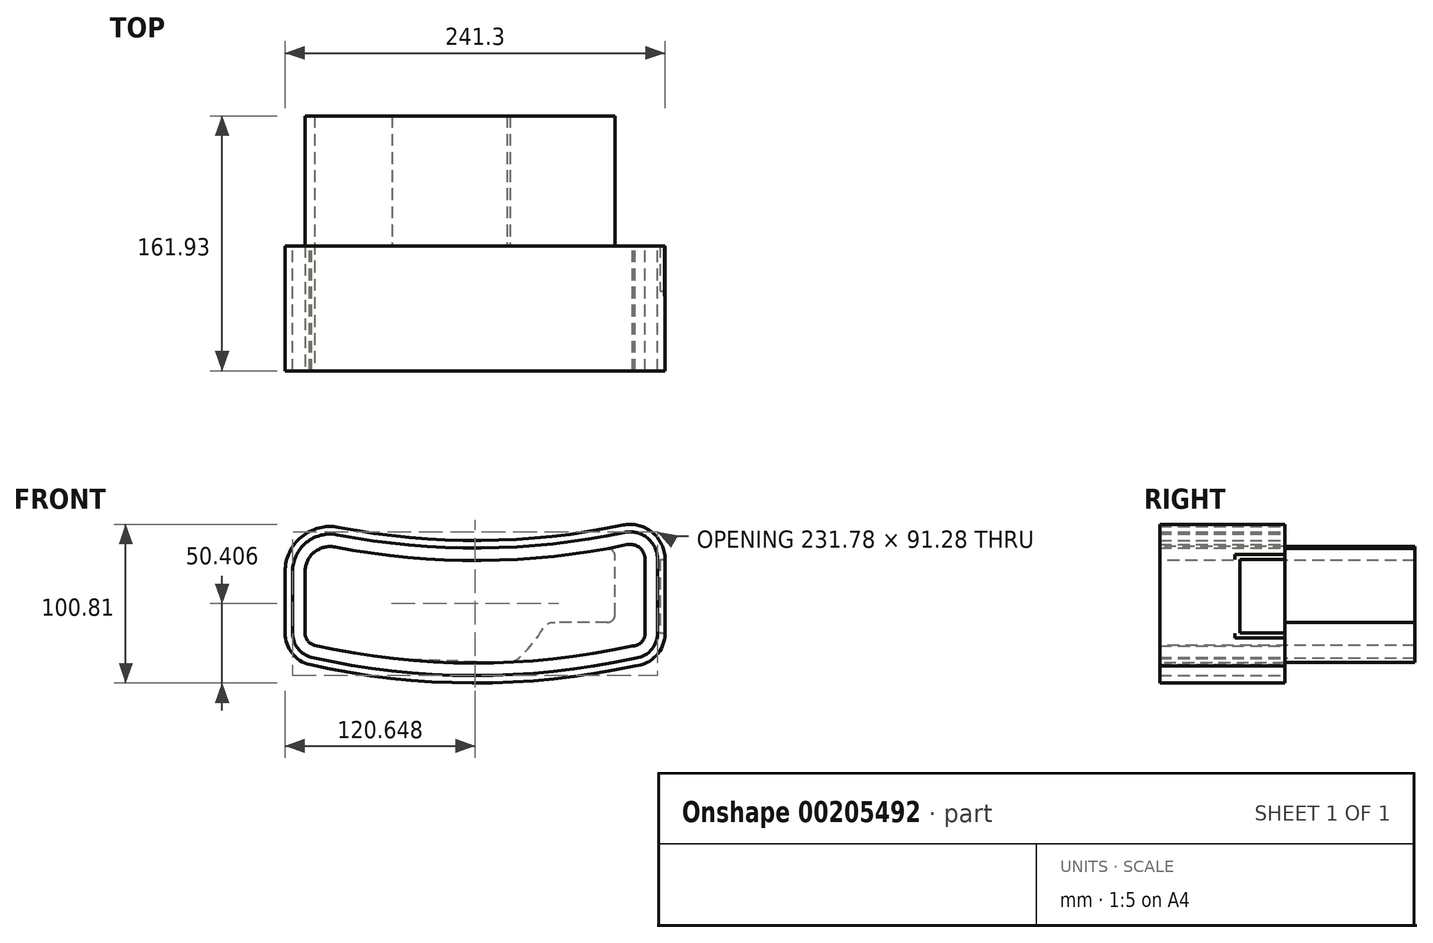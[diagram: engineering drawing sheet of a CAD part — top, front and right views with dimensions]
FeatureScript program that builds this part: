
annotation { "Feature Type Name" : "Feature", "Feature Type Description" : "" }
export const myFeature = defineFeature(function(context is Context, id is Id, definition is map)
    precondition{}
    {
        {
            var Q0;
            Q0=qCreatedBy(makeId("Front.planeOp"),FACE);
            var sketch = newSketch(context, id + "F0", { "sketchPlane" : qUnion([Q0])});
            skLineSegment(sketch, "E0", {"start": v(-57.08, 54.83) * mm, "end": v(-57.08, -10.26) * mm, "construction": true});
            skLineSegment(sketch, "E1", {"start": v(-57.08, 54.83) * mm, "end": v(158.82, 54.83) * mm, "construction": true});
            skLineSegment(sketch, "E2", {"start": v(50.87, 54.83) * mm, "end": v(50.87, 42.13) * mm, "construction": true});
            skArc(sketch, "E3", {"start": v(-57.08, 54.83) * mm, "mid": v(50.87, 42.13) * mm, "end": v(158.82, 54.83) * mm, "construction": true});
            skLineSegment(sketch, "E4", {"start": v(50.87, 42.13) * mm, "end": v(50.87, -22.96) * mm, "construction": true});
            skLineSegment(sketch, "E5", {"start": v(158.82, 54.83) * mm, "end": v(158.82, -10.26) * mm, "construction": true});
            skLineSegment(sketch, "E6", {"start": v(50.87, 42.13) * mm, "end": v(50.87, 13.56) * mm, "construction": true});
            skLineSegment(sketch, "E7", {"start": v(158.82, 22.29) * mm, "end": v(158.82, 9.59) * mm, "construction": true});
            skLineSegment(sketch, "E8", {"start": v(158.82, 9.59) * mm, "end": v(50.87, 13.56) * mm, "construction": true});
            skLineSegment(sketch, "E9", {"start": v(50.87, 13.56) * mm, "end": v(-57.08, 17.52) * mm, "construction": true});
            skLineSegment(sketch, "E10", {"start": v(-57.08, 35.15) * mm, "end": v(-57.08, -3.95) * mm});
            skLineSegment(sketch, "E11", {"start": v(158.82, 42.92) * mm, "end": v(158.82, -4.16) * mm});
            skArc(sketch, "E12", {"start": v(-38.17, 50.73) * mm, "mid": v(54.65, 42.15) * mm, "end": v(147.32, 52.24) * mm});
            skPoint(sketch, "E13.visualSharp", {"position": v(-57.08, 54.83) * mm});
            skArc(sketch, "E13.filletArc", {"start": v(-38.17, 50.73) * mm, "mid": v(-51.3, 47.4) * mm, "end": v(-57.08, 35.15) * mm});
            skPoint(sketch, "E14.visualSharp", {"position": v(158.82, 54.83) * mm});
            skArc(sketch, "E14.filletArc", {"start": v(158.82, 42.92) * mm, "mid": v(155.29, 50.32) * mm, "end": v(147.32, 52.24) * mm});
            skPoint(sketch, "E15.visualSharp", {"position": v(158.82, -10.26) * mm});
            skArc(sketch, "E15.filletArc", {"start": v(150.77, -12.1) * mm, "mid": v(156.45, -9.82) * mm, "end": v(158.82, -4.16) * mm});
            skPoint(sketch, "E16.visualSharp", {"position": v(-57.08, -10.26) * mm});
            skArc(sketch, "E16.filletArc", {"start": v(-57.08, -3.95) * mm, "mid": v(-55.43, -8.8) * mm, "end": v(-51.15, -11.63) * mm});
            skLineSegment(sketch, "E17", {"start": v(-57.08, 17.52) * mm, "end": v(-3.14, 15.54) * mm, "construction": true});
            skLineSegment(sketch, "E18", {"start": v(-3.14, 15.54) * mm, "end": v(-1.75, -19.97) * mm, "construction": true});
            skLineSegment(sketch, "E19", {"start": v(-3.14, 15.54) * mm, "end": v(69.83, 12.86) * mm, "construction": true});
            skLineSegment(sketch, "E20", {"start": v(69.83, 12.86) * mm, "end": v(71.22, -22.51) * mm, "construction": true});
            skLineSegment(sketch, "E21", {"start": v(-1.75, -19.97) * mm, "end": v(71.22, -22.51) * mm});
            skArc(sketch, "E22", {"start": v(-51.15, -11.63) * mm, "mid": v(-26.56, -16.47) * mm, "end": v(-1.75, -19.97) * mm});
            skArc(sketch, "E23.trimOffspring", {"start": v(71.22, -22.51) * mm, "mid": v(111.22, -19.02) * mm, "end": v(150.77, -12.1) * mm});
            skArc(sketch, "E24", {"start": v(-1.75, -19.97) * mm, "mid": v(34.69, -22.68) * mm, "end": v(71.22, -22.51) * mm});
            skLineSegment(sketch, "E25", {"start": v(71.22, -22.51) * mm, "end": v(71.22, 2.89) * mm, "construction": true});
            skLineSegment(sketch, "E26", {"start": v(-57.08, 2.89) * mm, "end": v(135, 2.89) * mm, "construction": true});
            skLineSegment(sketch, "E27", {"start": v(71.22, -22.51) * mm, "end": v(71.22, -6.64) * mm, "construction": true});
            skLineSegment(sketch, "E28", {"start": v(-57.08, 2.89) * mm, "end": v(101.67, 2.89) * mm, "construction": true});
            skLineSegment(sketch, "E29", {"start": v(71.22, -6.64) * mm, "end": v(101.67, -6.64) * mm, "construction": true});
            skLineSegment(sketch, "E30", {"start": v(101.67, 2.89) * mm, "end": v(101.67, -33.79) * mm, "construction": true});
            skLineSegment(sketch, "E31", {"start": v(135, 2.89) * mm, "end": v(101.67, 2.89) * mm});
            skLineSegment(sketch, "E32", {"start": v(139.77, 7.65) * mm, "end": v(139.77, 44.94) * mm});
            skLineSegment(sketch, "E33", {"start": v(139.77, 45.74) * mm, "end": v(108.7, 45.74) * mm, "construction": true});
            skArc(sketch, "E34", {"start": v(108.7, 45.74) * mm, "mid": v(121.45, 47.48) * mm, "end": v(134.14, 49.62) * mm});
            skPoint(sketch, "E35.visualSharp", {"position": v(139.77, 50.7) * mm});
            skArc(sketch, "E35.filletArc", {"start": v(139.77, 44.94) * mm, "mid": v(138.05, 48.6) * mm, "end": v(134.14, 49.62) * mm});
            skPoint(sketch, "E36.visualSharp", {"position": v(139.77, 2.89) * mm});
            skArc(sketch, "E36.filletArc", {"start": v(135, 2.89) * mm, "mid": v(138.37, 4.28) * mm, "end": v(139.77, 7.65) * mm});
            skLineSegment(sketch, "E37", {"start": v(90.61, -6.33) * mm, "end": v(102.06, -20.06) * mm, "construction": true});
            skLineSegment(sketch, "E38", {"start": v(78.3, -16.6) * mm, "end": v(79.93, -18.56) * mm, "construction": true});
            skLineSegment(sketch, "E39", {"start": v(96.3, 1.5) * mm, "end": v(96.3, -1.59) * mm, "construction": true});
            skFitSpline(sketch, "E40", {"points": [v(71.22, -22.51) * mm, v(79.93, -18.56) * mm, v(90.61, -6.33) * mm, v(96.3, 1.5) * mm, v(101.67, 2.89) * mm], "startDerivative": vector(48.06, -1.67) * mm, "endDerivative": vector(40.98, 0) * mm});
            skLineSegment(sketch, "E41", {"start": v(90.61, -6.33) * mm, "end": v(96.3, -1.59) * mm, "construction": true});
            skLineSegment(sketch, "E42", {"start": v(96.3, -1.59) * mm, "end": v(101.67, 2.89) * mm, "construction": true});
            skLineSegment(sketch, "E43", {"start": v(71.22, -22.51) * mm, "end": v(78.3, -16.6) * mm, "construction": true});
            skLineSegment(sketch, "E44", {"start": v(78.3, -16.6) * mm, "end": v(90.61, -6.33) * mm, "construction": true});
            skLineSegment(sketch, "E45.0", {"start": v(166.76, 42.92) * mm, "end": v(166.76, -4.16) * mm});
            skArc(sketch, "E45.1", {"start": v(151.73, -20.02) * mm, "mid": v(162.4, -15.08) * mm, "end": v(166.76, -4.16) * mm});
            skArc(sketch, "E45.2", {"start": v(166.76, 42.92) * mm, "mid": v(160.29, 56.5) * mm, "end": v(145.67, 60) * mm});
            skArc(sketch, "E45.3", {"start": v(71.51, -30.44) * mm, "mid": v(111.85, -26.95) * mm, "end": v(151.73, -20.02) * mm});
            skArc(sketch, "E45.4", {"start": v(-2.7, -27.85) * mm, "mid": v(34.35, -30.6) * mm, "end": v(71.51, -30.44) * mm});
            skArc(sketch, "E45.5", {"start": v(-53, -19.35) * mm, "mid": v(-27.97, -24.28) * mm, "end": v(-2.7, -27.85) * mm});
            skArc(sketch, "E45.6", {"start": v(-36.65, 58.52) * mm, "mid": v(54.59, 50.08) * mm, "end": v(145.67, 60) * mm});
            skArc(sketch, "E45.7", {"start": v(-36.65, 58.52) * mm, "mid": v(-56.35, 53.53) * mm, "end": v(-65.02, 35.15) * mm});
            skLineSegment(sketch, "E45.8", {"start": v(-65.02, 35.15) * mm, "end": v(-65.02, -3.95) * mm});
            skArc(sketch, "E45.9", {"start": v(-65.02, -3.95) * mm, "mid": v(-61.66, -13.72) * mm, "end": v(-53, -19.35) * mm});
            skArc(sketch, "E46.0", {"start": v(146.12, 44.94) * mm, "mid": v(142.11, 53.48) * mm, "end": v(132.98, 55.87) * mm});
            skArc(sketch, "E46.1", {"start": v(-63.43, -3.95) * mm, "mid": v(-60.41, -12.73) * mm, "end": v(-52.63, -17.8) * mm});
            skLineSegment(sketch, "E46.2", {"start": v(-63.43, 35.15) * mm, "end": v(-63.43, -3.95) * mm});
            skArc(sketch, "E46.3", {"start": v(-36.95, 56.96) * mm, "mid": v(-55.34, 52.3) * mm, "end": v(-63.43, 35.15) * mm});
            skArc(sketch, "E46.4", {"start": v(-36.95, 56.96) * mm, "mid": v(44.9, 48.52) * mm, "end": v(126.94, 54.83) * mm});
            skArc(sketch, "E46.5", {"start": v(-52.63, -17.8) * mm, "mid": v(-27.54, -22.74) * mm, "end": v(-2.21, -26.3) * mm});
            skLineSegment(sketch, "E46.6", {"start": v(-2.21, -26.3) * mm, "end": v(71, -28.86) * mm});
            skLineSegment(sketch, "E46.8", {"start": v(135, -3.46) * mm, "end": v(101.67, -3.46) * mm});
            skArc(sketch, "E46.9", {"start": v(135, -3.46) * mm, "mid": v(142.86, -0.2) * mm, "end": v(146.12, 7.65) * mm});
            skLineSegment(sketch, "E46.10", {"start": v(146.12, 7.65) * mm, "end": v(146.12, 44.94) * mm});
            skFitSpline(sketch, "E47.0", {"points": [v(71.06, -28.86) * mm, v(71.73, -28.88) * mm, v(73.06, -28.85) * mm, v(74.97, -28.57) * mm, v(76.77, -28.04) * mm, v(78.4, -27.3) * mm, v(79.86, -26.42) * mm, v(80.93, -25.62) * mm, v(81.73, -24.96) * mm, v(82.3, -24.46) * mm, v(82.85, -23.96) * mm, v(83.39, -23.45) * mm, v(83.93, -22.93) * mm, v(84.67, -22.2) * mm, v(85.61, -21.26) * mm, v(86.76, -20.07) * mm, v(88.3, -18.4) * mm, v(89.84, -16.66) * mm, v(91.33, -14.87) * mm, v(92.42, -13.51) * mm, v(93.3, -12.37) * mm, v(93.97, -11.46) * mm, v(94.46, -10.78) * mm, v(94.94, -10.1) * mm, v(95.53, -9.22) * mm, v(96.23, -8.17) * mm, v(96.97, -7.01) * mm, v(97.65, -5.98) * mm, v(98.25, -5.1) * mm, v(98.77, -4.4) * mm, v(99.11, -4) * mm, v(99.31, -3.8) * mm, v(99.42, -3.7) * mm, v(99.47, -3.67) * mm, v(99.5, -3.64) * mm, v(99.51, -3.64) * mm, v(99.62, -3.6) * mm, v(99.98, -3.53) * mm, v(100.65, -3.47) * mm, v(101.3, -3.46) * mm, v(101.67, -3.46) * mm]});
            skArc(sketch, "E48.0", {"start": v(-54.1, -23.98) * mm, "mid": v(-28.76, -28.98) * mm, "end": v(-3.18, -32.59) * mm});
            skArc(sketch, "E48.1", {"start": v(-69.78, -3.95) * mm, "mid": v(-65.4, -16.67) * mm, "end": v(-54.1, -23.98) * mm});
            skArc(sketch, "E48.2", {"start": v(-3.18, -32.59) * mm, "mid": v(34.25, -35.37) * mm, "end": v(71.78, -35.2) * mm});
            skLineSegment(sketch, "E48.3", {"start": v(-69.78, 35.15) * mm, "end": v(-69.78, -3.95) * mm});
            skArc(sketch, "E48.4", {"start": v(-35.74, 63.2) * mm, "mid": v(-59.38, 57.2) * mm, "end": v(-69.78, 35.15) * mm});
            skArc(sketch, "E48.5", {"start": v(-35.74, 63.2) * mm, "mid": v(54.55, 54.85) * mm, "end": v(144.68, 64.66) * mm});
            skArc(sketch, "E48.6", {"start": v(71.78, -35.2) * mm, "mid": v(112.31, -31.69) * mm, "end": v(152.4, -24.75) * mm});
            skArc(sketch, "E48.7", {"start": v(152.4, -24.75) * mm, "mid": v(166, -18.21) * mm, "end": v(171.52, -4.16) * mm});
            skLineSegment(sketch, "E48.8", {"start": v(171.52, 42.92) * mm, "end": v(171.52, -4.16) * mm});
            skArc(sketch, "E48.9", {"start": v(171.52, 42.92) * mm, "mid": v(163.28, 60.2) * mm, "end": v(144.68, 64.66) * mm});
            skArc(sketch, "E49.0", {"start": v(149.3, 44.94) * mm, "mid": v(144.14, 55.92) * mm, "end": v(132.4, 59) * mm});
            skArc(sketch, "E49.1", {"start": v(-79.54, -6.52) * mm, "mid": v(-75.84, -17.27) * mm, "end": v(-66.3, -23.46) * mm});
            skLineSegment(sketch, "E49.2", {"start": v(-79.54, 32.58) * mm, "end": v(-79.54, -6.52) * mm});
            skArc(sketch, "E49.3", {"start": v(-49.28, 57.51) * mm, "mid": v(-70.3, 52.19) * mm, "end": v(-79.54, 32.58) * mm});
            skArc(sketch, "E49.4", {"start": v(-49.28, 57.51) * mm, "mid": v(41.64, 49.1) * mm, "end": v(132.4, 59) * mm});
            skArc(sketch, "E49.5", {"start": v(-66.3, -23.46) * mm, "mid": v(-40.96, -28.45) * mm, "end": v(-15.39, -32.05) * mm});
            skLineSegment(sketch, "E49.6", {"start": v(-15.39, -32.05) * mm, "end": v(57.96, -34.6) * mm});
            skLineSegment(sketch, "E49.8", {"start": v(135, -6.64) * mm, "end": v(102.16, -6.64) * mm});
            skArc(sketch, "E49.9", {"start": v(135, -6.64) * mm, "mid": v(145.1, -2.45) * mm, "end": v(149.3, 7.65) * mm});
            skLineSegment(sketch, "E49.10", {"start": v(149.3, 7.65) * mm, "end": v(149.3, 44.94) * mm});
            skFitSpline(sketch, "E50", {"points": [v(71.78, -35.2) * mm, v(77.2, -34.93) * mm, v(85.03, -26.96) * mm, v(93.69, -17.23) * mm, v(99.13, -10.11) * mm, v(101.67, -6.64) * mm], "startDerivative": vector(31.28, -0.44) * mm, "endDerivative": vector(15.72, 21.75) * mm});
            skArc(sketch, "E51.filletArc", {"start": v(102.16, -6.64) * mm, "mid": v(101.72, -6.74) * mm, "end": v(101.38, -7.03) * mm});
            skLineSegment(sketch, "E52", {"start": v(126.94, 54.83) * mm, "end": v(132.98, 55.87) * mm});
            skSolve(sketch);
        }
        {
            var Q0;
            Q0=makeQuery(id+"F0.imprint","IMPRINT",FACE,{"disambiguationData":[TD([[makeQuery(id+"F0.imprint","IMPRINT",EDGE,{"derivedFrom":sQuery(id+"F0.wireOp",EDGE,"E10")}),1.0]])]});
            extrude(context, id + "F1", {"entities" : qUnion([Q0]), "oppositeDirection" : true, "depth" : 82.55 * mm});
        }
        {
            var Q0;
            Q0=makeQuery(id+"F0.imprint","IMPRINT",FACE,{"disambiguationData":[TD([[makeQuery(id+"F0.imprint","IMPRINT",EDGE,{"derivedFrom":sQuery(id+"F0.wireOp",EDGE,"E11")}),-1.0]])]});
            var Q1;
            Q1=makeQuery(id+"F0.imprint","IMPRINT",FACE,{"disambiguationData":[TD([[makeQuery(id+"F0.imprint","IMPRINT",EDGE,{"derivedFrom":sQuery(id+"F0.wireOp",EDGE,"E10")}),1.0]])]});
            var Q2;
            Q2=makeQuery(id+"F0.imprint","IMPRINT",FACE,{"disambiguationData":[TD([[makeQuery(id+"F0.imprint","IMPRINT",EDGE,{"derivedFrom":sQuery(id+"F0.wireOp",EDGE,"E21")}),-1.0]])]});
            var Q3;
            {var subQ1=sQuery(id+"F0.wireOp",EDGE,"E31");Q3=makeQuery(id+"F0.imprint","IMPRINT",FACE,{"disambiguationData":[TD([[makeQuery(id+"F0.imprint","IMPRINT",EDGE,{"derivedFrom":subQ1}),1.0]])]});}
            var Q4;
            {var subQ5=sQuery(id+"F0.wireOp",EDGE,"E46.8");Q4=makeQuery(id+"F0.imprint","IMPRINT",FACE,{"disambiguationData":[TD([[makeQuery(id+"F0.imprint","IMPRINT",EDGE,{"derivedFrom":subQ5}),1.0]])]});}
            extrude(context, id + "F2", {"entities" : qUnion([Q0, Q1, Q2, Q3, Q4]), "operationType" : NewBodyOperationType.ADD, "depth" : 79.38 * mm});
        }
        {
            var Q0;
            Q0=makeQuery(id+"F0.imprint","IMPRINT",FACE,{"disambiguationData":[TD([[makeQuery(id+"F0.imprint","IMPRINT",EDGE,{"derivedFrom":sQuery(id+"F0.wireOp",EDGE,"E45.0")}),1.0]])]});
            var Q1;
            {var subQ0=sQuery(id+"F0.wireOp",EDGE,"E49.4");var subQ1=sQuery(id+"F0.wireOp",EDGE,"E45.6");var subQ2=makeQuery(id+"F0.imprint","INTERSECT",VERTEX,{"derivedFrom":[subQ1,subQ0]});Q1=makeQuery(id+"F0.imprint","IMPRINT",FACE,{"disambiguationData":[TD([[makeQuery(id+"F0.imprint","IMPRINT",EDGE,{"disambiguationData":[TD([[subQ2,-1.0]])],"derivedFrom":subQ1}),1.0]])]});}
            var Q2;
            {var subQ10=sQuery(id+"F0.wireOp",EDGE,"E45.4");Q2=makeQuery(id+"F0.imprint","IMPRINT",FACE,{"disambiguationData":[TD([[makeQuery(id+"F0.imprint","IMPRINT",EDGE,{"derivedFrom":subQ10}),-1.0]])]});}
            var Q3;
            Q3=makeQuery(id+"F2.opExtrude","CAP_FACE",FACE,{"disambiguationData":[OSD([sQuery(id+"F0.wireOp",EDGE,"E10"),sQuery(id+"F0.wireOp",EDGE,"E11"),sQuery(id+"F0.wireOp",EDGE,"E12"),sQuery(id+"F0.wireOp",EDGE,"E13.filletArc"),sQuery(id+"F0.wireOp",EDGE,"E14.filletArc"),sQuery(id+"F0.wireOp",EDGE,"E15.filletArc"),sQuery(id+"F0.wireOp",EDGE,"E16.filletArc"),sQuery(id+"F0.wireOp",EDGE,"E22"),sQuery(id+"F0.wireOp",EDGE,"E23.trimOffspring"),sQuery(id+"F0.wireOp",EDGE,"E24")])],"isStart":false});
            extrude(context, id + "F3", {"entities" : qUnion([Q0, Q1, Q2]), "endBound" : BoundingType.UP_TO_SURFACE, "endBoundEntityFace" : qUnion([Q3]), "depth" : 25.4 * mm});
        }
        {
            var Q0;
            Q0=makeQuery(id+"F3.opExtrude","SWEPT_FACE",FACE,{"disambiguationData":[OSD([sQuery(id+"F0.wireOp",EDGE,"E48.8")])]});
            var sketch = newSketch(context, id + "F4", { "sketchPlane" : qUnion([Q0])});
            skLineSegment(sketch, "E53", {"start": v(0, -3.95) * mm, "end": v(-28.58, -3.95) * mm, "construction": true});
            skLineSegment(sketch, "E54.bottom", {"start": v(0, 42.92) * mm, "end": v(-28.58, 42.92) * mm});
            skLineSegment(sketch, "E54.top", {"start": v(0, -3.95) * mm, "end": v(-28.58, -3.95) * mm});
            skLineSegment(sketch, "E54.left", {"start": v(0, 42.92) * mm, "end": v(0, -3.95) * mm});
            skLineSegment(sketch, "E54.right", {"start": v(-28.58, 42.92) * mm, "end": v(-28.58, -3.95) * mm});
            skLineSegment(sketch, "E55.0", {"start": v(0, -7.13) * mm, "end": v(-31.75, -7.13) * mm});
            skLineSegment(sketch, "E55.1", {"start": v(-31.75, 46.1) * mm, "end": v(-31.75, -7.13) * mm});
            skLineSegment(sketch, "E55.2", {"start": v(0, 46.1) * mm, "end": v(-31.75, 46.1) * mm});
            skLineSegment(sketch, "E56", {"start": v(0, 46.1) * mm, "end": v(0, 42.92) * mm});
            skLineSegment(sketch, "E57", {"start": v(0, -3.95) * mm, "end": v(0, -7.13) * mm});
            skLineSegment(sketch, "E58.0", {"start": v(-79.38, 42.92) * mm, "end": v(-79.38, -4.16) * mm});
            skLineSegment(sketch, "E59.0", {"start": v(82.55, 7.65) * mm, "end": v(82.55, 44.94) * mm});
            skSolve(sketch);
        }
        {
            var Q0;
            Q0=makeQuery(id+"F4.imprint","IMPRINT",FACE,{"disambiguationData":[TD([[makeQuery(id+"F4.imprint","IMPRINT",EDGE,{"derivedFrom":sQuery(id+"F4.wireOp",EDGE,"E54.bottom")}),-1.0]])]});
            extrude(context, id + "F5", {"entities" : qUnion([Q0]), "operationType" : NewBodyOperationType.REMOVE, "oppositeDirection" : true, "depth" : 3.17 * mm});
        }
        {
            var Q0;
            {var subQ4=sQuery(id+"F4.wireOp",EDGE,"E54.bottom");Q0=makeQuery(id+"F4.imprint","IMPRINT",FACE,{"disambiguationData":[TD([[makeQuery(id+"F4.imprint","IMPRINT",EDGE,{"derivedFrom":subQ4}),1.0]])]});}
            var Q1;
            {var subQ4=sQuery(id+"F4.wireOp",EDGE,"E54.top");Q1=makeQuery(id+"F4.imprint","IMPRINT",FACE,{"disambiguationData":[TD([[makeQuery(id+"F4.imprint","IMPRINT",EDGE,{"derivedFrom":subQ4}),1.0]])]});}
            var Q2;
            {var subQ0=sQuery(id+"F4.wireOp",EDGE,"E55.0");Q2=makeQuery(id+"F4.imprint","IMPRINT",FACE,{"disambiguationData":[TD([[makeQuery(id+"F4.imprint","IMPRINT",EDGE,{"derivedFrom":subQ0}),-1.0]])]});}
            extrude(context, id + "F6", {"entities" : qUnion([Q0, Q1, Q2]), "operationType" : NewBodyOperationType.ADD, "oppositeDirection" : true, "depth" : 2.54 * mm});
        }
        {
            var Q0;
            Q0=sQuery(id+"F4.wireOp",EDGE,"E55.1");
            var Q1;
            Q1=sQuery(id+"FjQQDPw6VX4Te0q_2.wireOp",EDGE,"A7wqRoM7-RVCN-5NiP-FK9i-prnwNeDVTaok");
            cPlane(context, id + "F7", {"entities" : qUnion([Q0, Q1]), "cplaneType" : CPlaneType.LINE_ANGLE, "offset" : 25.4 * mm, "angle" : 0 * degree, "width" : 152.4 * mm, "height" : 152.4 * mm});
        }
    });
